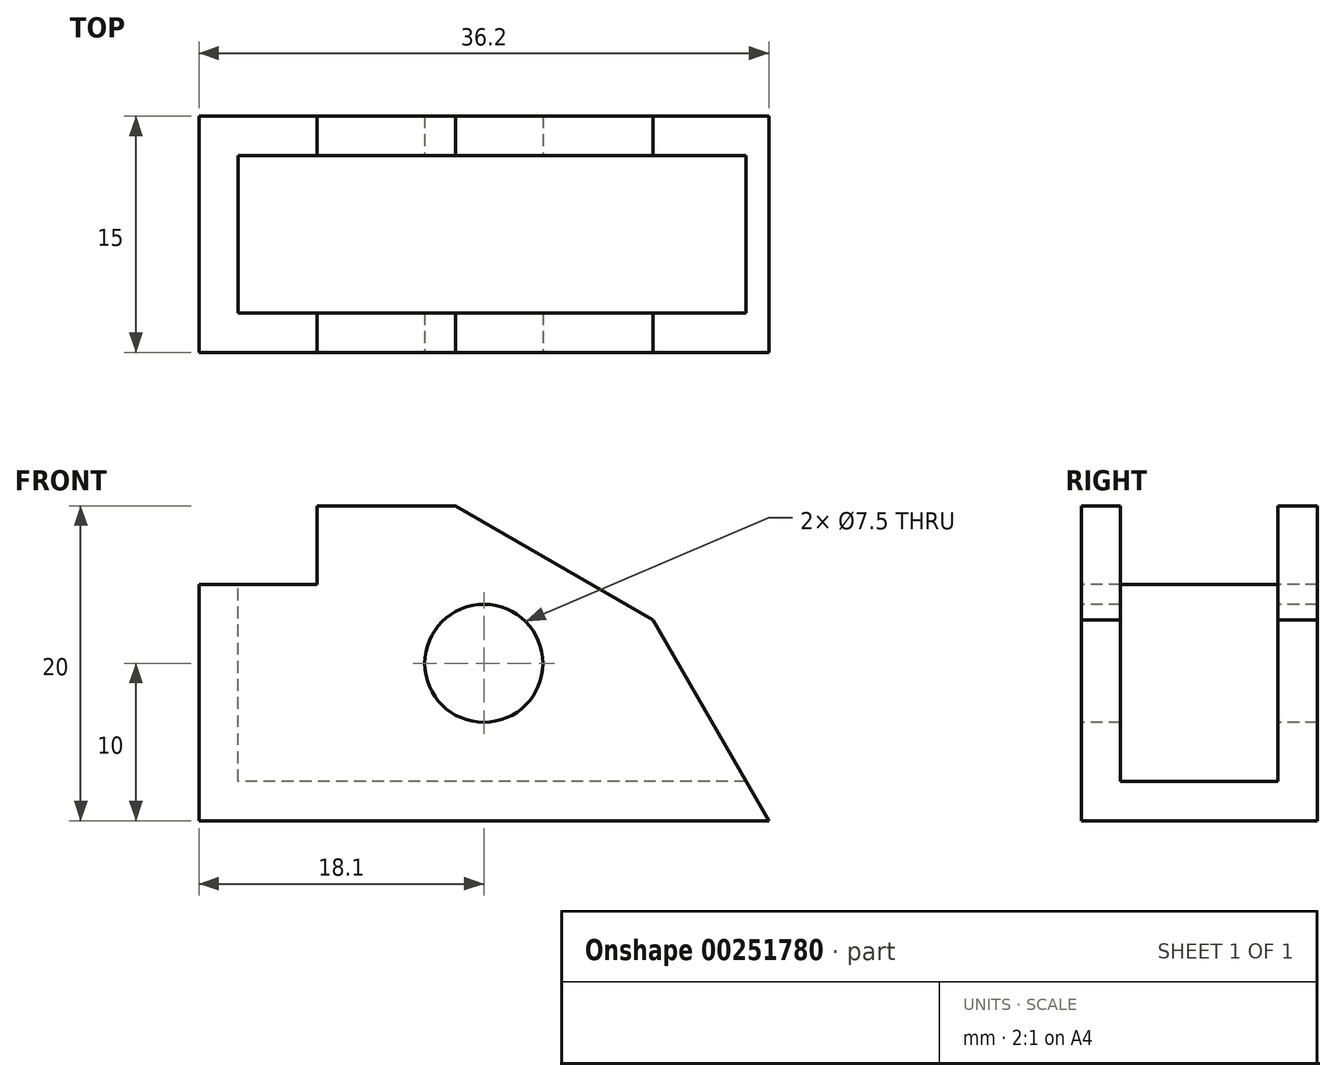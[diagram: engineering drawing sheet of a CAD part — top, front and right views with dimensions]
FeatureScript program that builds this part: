
annotation { "Feature Type Name" : "Feature", "Feature Type Description" : "" }
export const myFeature = defineFeature(function(context is Context, id is Id, definition is map)
    precondition{}
    {
        {
            var Q0;
            Q0=qCreatedBy(makeId("Front.planeOp"),FACE);
            var sketch = newSketch(context, id + "F0", { "sketchPlane" : qUnion([Q0])});
            skLineSegment(sketch, "E0.bottom", {"start": v(-10.6, 10) * mm, "end": v(-1.8, 10) * mm});
            skLineSegment(sketch, "E0.top", {"start": v(-18.1, -10) * mm, "end": v(18.1, -10) * mm});
            skLineSegment(sketch, "E0.left", {"start": v(-18.1, 5) * mm, "end": v(-18.1, -10) * mm});
            skPoint(sketch, "E0.middle", {"position": v(0, 0) * mm});
            skLineSegment(sketch, "E1", {"start": v(18.1, -10) * mm, "end": v(10.73, 2.77) * mm});
            skLineSegment(sketch, "E2", {"start": v(-18.1, 5) * mm, "end": v(-10.6, 5) * mm});
            skLineSegment(sketch, "E3", {"start": v(-10.6, 5) * mm, "end": v(-10.6, 10) * mm});
            skPoint(sketch, "E4.orphan", {"position": v(-18.1, 10) * mm});
            skLineSegment(sketch, "E5", {"start": v(-18.1, 17) * mm, "end": v(-1.8, 17) * mm});
            skLineSegment(sketch, "E6", {"start": v(-1.8, 10) * mm, "end": v(10.73, 2.77) * mm});
            skPoint(sketch, "E0.right.start.orphan", {"position": v(18.1, 10) * mm});
            skSolve(sketch);
        }
        {
            var Q0;
            Q0 = qSketchRegion(id + "F0", true);
            extrude(context, id + "F1", {"entities" : qUnion([Q0]), "oppositeDirection" : true, "depth" : 15 * mm});
        }
        {
            var Q0;
            Q0=makeQuery(id+"F1.opExtrude","SWEPT_FACE",FACE,{"disambiguationData":[OSD([sQuery(id+"F0.wireOp",EDGE,"E0.left")])]});
            var sketch = newSketch(context, id + "F2", { "sketchPlane" : qUnion([Q0])});
            skLineSegment(sketch, "E7.top", {"start": v(-2.5, 21) * mm, "end": v(-12.5, 21) * mm});
            skLineSegment(sketch, "E7.left", {"start": v(-2.5, -7.5) * mm, "end": v(-2.5, 21) * mm});
            skLineSegment(sketch, "E7.right", {"start": v(-12.5, -7.5) * mm, "end": v(-12.5, 21) * mm});
            skPoint(sketch, "E7.middle", {"position": v(-7.5, -2.5) * mm});
            skPoint(sketch, "E7.middle.positionSnap0", {"position": v(-7.5, -10) * mm});
            skPoint(sketch, "E7.middle.positionSnap1", {"position": v(-15, -2.5) * mm});
            skPoint(sketch, "E7.centerSnap0", {"position": v(-7.5, -10) * mm});
            skPoint(sketch, "E7.centerSnap1", {"position": v(-15, -2.5) * mm});
            skLineSegment(sketch, "E8", {"start": v(-12.5, -7.5) * mm, "end": v(-2.5, -7.5) * mm});
            skPoint(sketch, "E9.orphan", {"position": v(-12.5, -26) * mm});
            skPoint(sketch, "E10.orphan", {"position": v(-2.5, -26) * mm});
            skSolve(sketch);
        }
        {
            var Q0;
            Q0 = qSketchRegion(id + "F2", true);
            extrude(context, id + "F3", {"entities" : qUnion([Q0]), "operationType" : NewBodyOperationType.REMOVE, "endBound" : BoundingType.THROUGH_ALL, "oppositeDirection" : true, "depth" : 10 * mm});
        }
        {
            var Q0;
            Q0=makeQuery(id+"F1.opExtrude","SWEPT_FACE",FACE,{"disambiguationData":[OSD([sQuery(id+"F0.wireOp",EDGE,"E0.left")])]});
            var sketch = newSketch(context, id + "F4", { "sketchPlane" : qUnion([Q0])});
            skLineSegment(sketch, "E11", {"start": v(-12.5, 5) * mm, "end": v(-2.5, 5) * mm});
            skLineSegment(sketch, "E12.0", {"start": v(-12.5, -7.5) * mm, "end": v(-2.5, -7.5) * mm});
            skLineSegment(sketch, "E13.0", {"start": v(-2.5, -7.5) * mm, "end": v(-2.5, 5) * mm});
            skLineSegment(sketch, "E14.0", {"start": v(-12.5, -7.5) * mm, "end": v(-12.5, 5) * mm});
            skSolve(sketch);
        }
        {
            var Q0;
            Q0 = qSketchRegion(id + "F4", true);
            extrude(context, id + "F5", {"entities" : qUnion([Q0]), "operationType" : NewBodyOperationType.ADD, "oppositeDirection" : true, "depth" : 2.5 * mm});
        }
        {
            var Q0;
            Q0=makeQuery(id+"F1.opExtrude","CAP_FACE",FACE,{"disambiguationData":[OSD([sQuery(id+"F0.wireOp",EDGE,"E0.bottom"),sQuery(id+"F0.wireOp",EDGE,"E0.top"),sQuery(id+"F0.wireOp",EDGE,"E0.left"),sQuery(id+"F0.wireOp",EDGE,"E1"),sQuery(id+"F0.wireOp",EDGE,"E2"),sQuery(id+"F0.wireOp",EDGE,"E3"),sQuery(id+"F0.wireOp",EDGE,"E6")])],"isStart":true});
            var sketch = newSketch(context, id + "F6", { "sketchPlane" : qUnion([Q0])});
            skCircle(sketch, "E15", {"center": v(0, 0) * mm, "radius": 3.75 * mm});
            skSolve(sketch);
        }
        {
            var Q0;
            Q0 = qSketchRegion(id + "F6", true);
            extrude(context, id + "F7", {"entities" : qUnion([Q0]), "operationType" : NewBodyOperationType.REMOVE, "endBound" : BoundingType.THROUGH_ALL, "oppositeDirection" : true, "depth" : 25 * mm});
        }
    });
